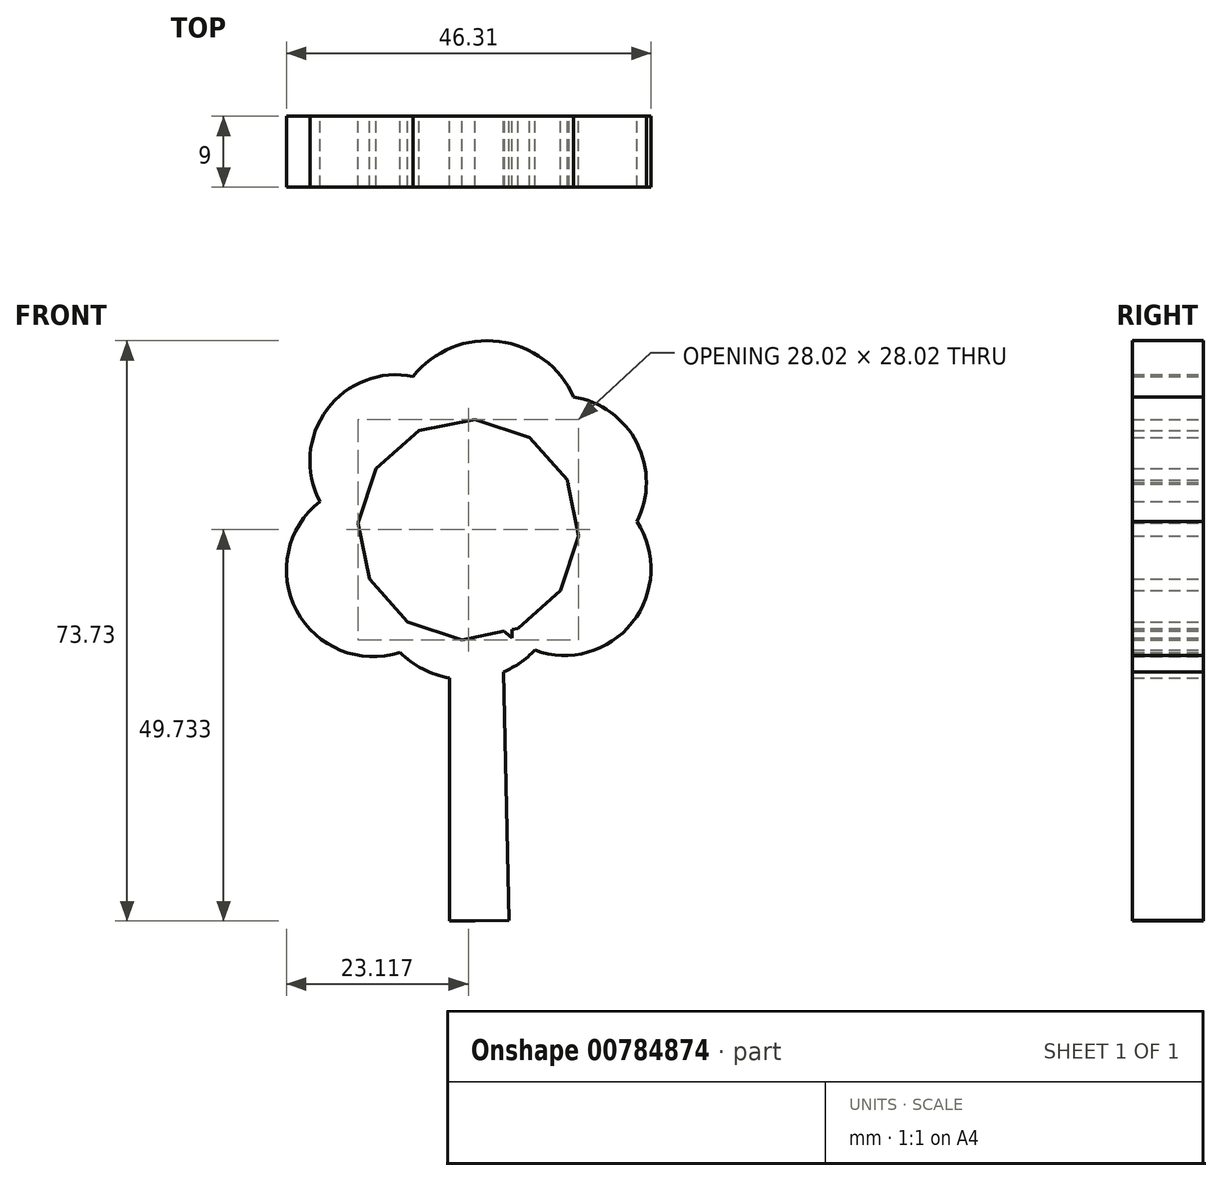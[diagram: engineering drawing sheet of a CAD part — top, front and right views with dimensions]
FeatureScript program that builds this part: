
annotation { "Feature Type Name" : "Feature", "Feature Type Description" : "" }
export const myFeature = defineFeature(function(context is Context, id is Id, definition is map)
    precondition{}
    {
        {
            var Q0;
            Q0=qCreatedBy(makeId("Front.planeOp"),FACE);
            var sketch = newSketch(context, id + "F0", { "sketchPlane" : qUnion([Q0])});
            skPoint(sketch, "E0.middle", {"position": v(0, 0) * mm});
            skPoint(sketch, "E1.orphan", {"position": v(0, 18.23) * mm});
            skPoint(sketch, "E2.orphan", {"position": v(0, 60.6) * mm});
            skPoint(sketch, "E3.center.orphan", {"position": v(0, 33.23) * mm});
            skPoint(sketch, "E0.left.start.orphan", {"position": v(-3.23, 19.22) * mm});
            skLineSegment(sketch, "E4", {"start": v(1.54, 19.22) * mm, "end": v(-3.23, 19.22) * mm});
            skCircle(sketch, "E5.cCircle", {"center": v(-0.84, 19.22) * mm, "radius": 14.03 * mm, "construction": true});
            skLineSegment(sketch, "E5.0", {"start": v(0, 33.23) * mm, "end": v(6.9, 30.93) * mm});
            skLineSegment(sketch, "E5.1", {"start": v(6.9, 30.93) * mm, "end": v(11.71, 25.5) * mm});
            skLineSegment(sketch, "E5.2", {"start": v(11.71, 25.5) * mm, "end": v(13.17, 18.38) * mm});
            skLineSegment(sketch, "E5.3", {"start": v(13.17, 18.38) * mm, "end": v(10.87, 11.49) * mm});
            skLineSegment(sketch, "E5.4", {"start": v(10.87, 11.49) * mm, "end": v(5.43, 6.67) * mm});
            skLineSegment(sketch, "E5.5", {"start": v(5.43, 6.67) * mm, "end": v(-1.69, 5.21) * mm});
            skLineSegment(sketch, "E5.6", {"start": v(-1.69, 5.21) * mm, "end": v(-8.58, 7.51) * mm});
            skLineSegment(sketch, "E5.7", {"start": v(-8.58, 7.51) * mm, "end": v(-13.4, 12.95) * mm});
            skLineSegment(sketch, "E5.8", {"start": v(-13.4, 12.95) * mm, "end": v(-14.85, 20.07) * mm});
            skLineSegment(sketch, "E5.9", {"start": v(-14.85, 20.07) * mm, "end": v(-12.55, 26.96) * mm});
            skLineSegment(sketch, "E5.10", {"start": v(-12.55, 26.96) * mm, "end": v(-7.12, 31.78) * mm});
            skLineSegment(sketch, "E5.11", {"start": v(-7.12, 31.78) * mm, "end": v(0, 33.23) * mm});
            skArc(sketch, "E6", {"start": v(-3.23, 19.22) * mm, "mid": v(-23.84, 15.7) * mm, "end": v(-5.13, 6.36) * mm});
            skArc(sketch, "E7", {"start": v(0, 32.5) * mm, "mid": v(-20.68, 30.5) * mm, "end": v(-3.23, 19.22) * mm});
            skPoint(sketch, "E7.startSnap0", {"position": v(-3.56, 32.5) * mm});
            skArc(sketch, "E8", {"start": v(4.7, 19.65) * mm, "mid": v(7.42, 41.69) * mm, "end": v(-9.99, 27.9) * mm});
            skArc(sketch, "E9", {"start": v(4.7, 16.04) * mm, "mid": v(21.53, 27.46) * mm, "end": v(1.54, 31.22) * mm});
            skArc(sketch, "E10", {"start": v(1.54, 19.22) * mm, "mid": v(17.35, 5.02) * mm, "end": v(10.76, 25.22) * mm});
            skArc(sketch, "E11", {"start": v(-12.96, 14.1) * mm, "mid": v(-2.42, 0.24) * mm, "end": v(10.87, 11.49) * mm});
            skLineSegment(sketch, "E12", {"start": v(-0.6, 5.43) * mm, "end": v(-0.6, 5.2) * mm});
            skLineSegment(sketch, "E13", {"start": v(-3.23, -30.51) * mm, "end": v(0, -30.51) * mm});
            skLineSegment(sketch, "E14", {"start": v(4.7, 1.67) * mm, "end": v(4.7, 6.52) * mm});
            skLineSegment(sketch, "E15", {"start": v(-3.23, 19.22) * mm, "end": v(-3.23, -30.51) * mm});
            skPoint(sketch, "E16.orphan", {"position": v(-5.76, -30.51) * mm});
            skLineSegment(sketch, "E17", {"start": v(0, -30.51) * mm, "end": v(4.28, -30.44) * mm});
            skLineSegment(sketch, "E18", {"start": v(0, 18.23) * mm, "end": v(3.24, 19.65) * mm});
            skLineSegment(sketch, "E19", {"start": v(3.24, 19.65) * mm, "end": v(4.28, -30.44) * mm});
            skArc(sketch, "E20.trimOffspring", {"start": v(2.43, 7.8) * mm, "mid": v(2.96, 7.97) * mm, "end": v(3.48, 8.16) * mm});
            skSolve(sketch);
        }
        {
            var Q0;
            Q0 = qSketchRegion(id + "F0", true);
            extrude(context, id + "F1", {"entities" : qUnion([Q0]), "depth" : 9 * mm, "offsetDistance" : 25 * mm});
        }
    });
